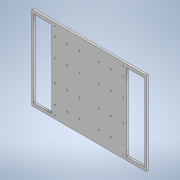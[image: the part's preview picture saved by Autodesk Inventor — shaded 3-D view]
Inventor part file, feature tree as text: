
AUTODESK INVENTOR PART (.ipt)
format: ipt  version: 2020.1 (Build 241239000, 239)  size: 231,936 bytes
history: native  units: mm
features: sketch x4, fillet x3, extrude x2, hole x2
ambient origin geometry x8: Origin, YZ Plane, XZ Plane, XY Plane, X Axis, Y Axis, Z Axis, Center Point
bodies: Solid1 (feature_tree)
feature tree (11):
  extrude  "Extrusion1"  Depth=270.0mm
  fillet  "Fillet1"  Radius=6.0mm
  fillet  "Fillet2"  Radius=2.0mm
  extrude  "Extrusion2"  Depth=60.0mm
  fillet  "Fillet3"  Radius=60.0mm
  hole  "Hole1"  [1 undecoded]
  hole  "Hole2"  [1 undecoded]
  sketch  "Sketch1"  dims[d0=371.6mm d1=270.0mm d2=6.0mm d3=0.0mm d4=2.0mm]
  sketch  "Sketch2"  dims[d5=2.0mm d6=60.0mm d7=60.0mm]
  sketch  "Sketch3"  dims[d8=250.0mm d9=250.0mm]
  sketch  "Sketch4"  dims[d10=65.0mm d11=10.0mm d12=10.0mm d13=65.0mm d14=0.0mm d15=0.0mm d16=2.0mm d17=10.0mm d18=40.0mm d19=40.0mm d20=10.0mm d22=40.0mm d23=40.0mm d24=30.0mm d25=30.0mm d26=30.0mm d27=30.0mm d28=30.0mm d29=30.0mm d30=60.0mm d31=10.0mm d32=60.0mm d33=60.0mm d34=40.0mm d35=40.0mm d36=40.0mm d37=40.0mm d38=10.0mm d39=60.0mm d40=60.0mm d41=60.0mm d42=10.0mm d43=10.0mm d45=60.0mm d46=40.0mm d47=40.0mm d48=40.0mm d49=40.0mm d50=10.0mm d51=10.0mm d52=40.0mm d53=40.0mm d54=40.0mm d55=40.0mm d56=30.0mm d57=60.0mm d58=60.0mm d59=60.0mm d60=60.0mm d61=60.0mm d62=30.0mm d63=30.0mm d64=30.0mm d65=30.0mm d66=30.0mm d67=3.3mm d68=6.0mm d69=4.0mm d70=2.0mm d71=90.0deg d72=8.0mm d73=20.594885mm d74=3.0mm d75=10.0mm d76=10.0mm d77=10.0mm d78=3.0mm d79=10.0mm d80=10.0mm d81=10.0mm d82=10.0mm d83=10.0mm d84=3.0mm d85=6.0mm d86=4.0mm d87=2.0mm d88=90.0deg d89=8.0mm d90=20.594885mm]
note: 2 required parameter values undecoded (feature->parameter linkage not recoverable at this tier; creation-order binding heuristic only, values carry confidence <= 0.55)
